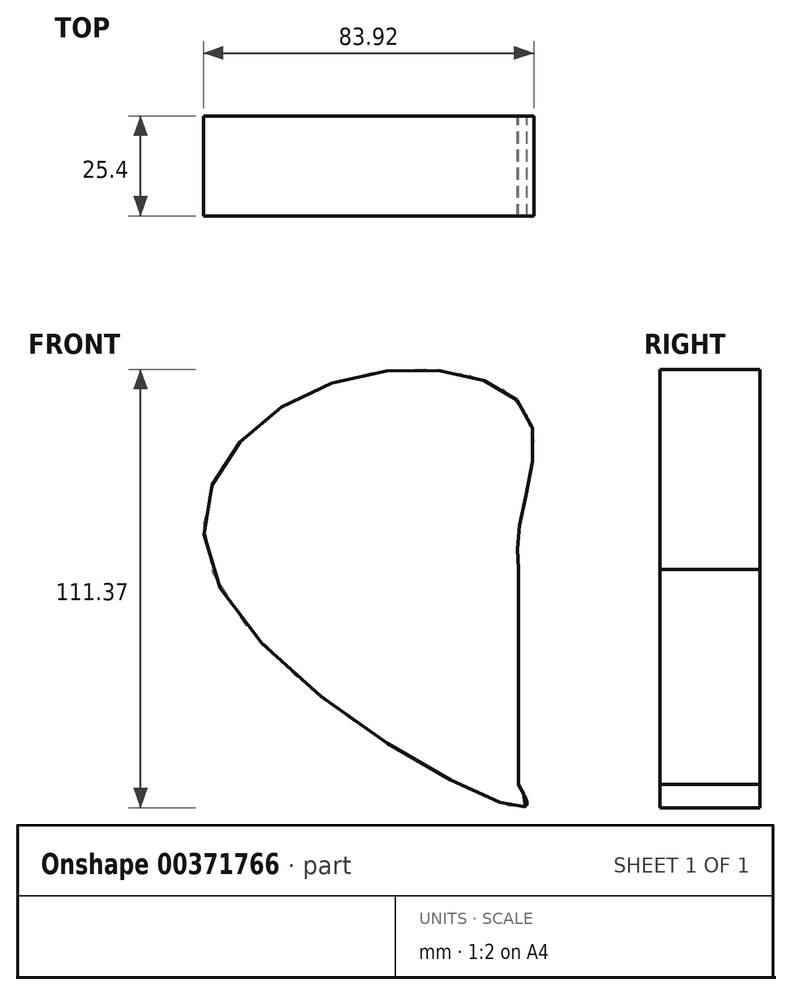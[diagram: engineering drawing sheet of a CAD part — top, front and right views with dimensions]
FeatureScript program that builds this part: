
annotation { "Feature Type Name" : "Feature", "Feature Type Description" : "" }
export const myFeature = defineFeature(function(context is Context, id is Id, definition is map)
    precondition{}
    {
        {
            var Q0;
            Q0=qCreatedBy(makeId("Front.planeOp"),FACE);
            var sketch = newSketch(context, id + "F0", { "sketchPlane" : qUnion([Q0])});
            skFitSpline(sketch, "E0", {"points": [v(0, 0) * mm, v(-6.47, 34.45) * mm, v(-43.3, 38.95) * mm, v(-57.09, 0) * mm, v(0, -55.82) * mm, v(0, -54.7) * mm], "startDerivative": vector(8.36, 191.97) * mm, "endDerivative": vector(-15.02, 42.24) * mm});
            skSolve(sketch);
        }
        {
            var Q0;
            Q0=qCreatedBy(makeId("Front.planeOp"),FACE);
            var sketch = newSketch(context, id + "F1", { "sketchPlane" : qUnion([Q0])});
            skLineSegment(sketch, "E1", {"start": v(0, -55.82) * mm, "end": v(0, 0) * mm});
            skLineSegment(sketch, "E2", {"start": v(0, 0) * mm, "end": v(0, 18.42) * mm});
            skSolve(sketch);
        }
        {
            var Q0;
            Q0=qCreatedBy(makeId("Front.planeOp"),FACE);
            var sketch = newSketch(context, id + "F2", { "sketchPlane" : qUnion([Q0])});
            skFitSpline(sketch, "E3.0", {"points": [v(0, 0) * mm, v(0.58, 13.32) * mm, v(1.76, 40.35) * mm, v(-48.32, 46.98) * mm, v(-76.94, -2.57) * mm, v(1.95, -60.17) * mm, v(0.19, -55.22) * mm, v(0, -54.7) * mm]});
            skLineSegment(sketch, "E3.1", {"start": v(0, -55.82) * mm, "end": v(0, 0) * mm});
            skSolve(sketch);
        }
        {
            var Q0;
            {var subQ0=sQuery(id+"F2.wireOp",EDGE,"E3.1");var subQ1=sQuery(id+"F2.wireOp",EDGE,"E3.0");var subQ2=makeQuery(id+"F2.imprint","INTERSECT",VERTEX,{"disambiguationData":[OD(0.0)],"derivedFrom":[subQ1,subQ0]});Q0=makeQuery(id+"F2.imprint","IMPRINT",FACE,{"disambiguationData":[TD([[makeQuery(id+"F2.imprint","IMPRINT",EDGE,{"disambiguationData":[TD([[subQ2,-1.0]])],"derivedFrom":subQ1}),1.0]])]});}
            extrude(context, id + "F3", {"entities" : qUnion([Q0]), "depth" : 25.4 * mm});
        }
    });
